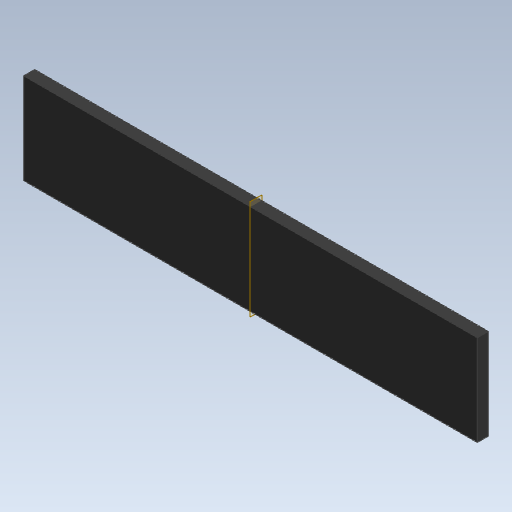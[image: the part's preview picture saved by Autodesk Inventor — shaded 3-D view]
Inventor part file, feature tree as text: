
AUTODESK INVENTOR PART (.ipt)
format: ipt  version: 2020 (Build 240168000, 168)  size: 105,472 bytes
history: native  units: mm
features: other x1, extrude x1
ambient origin geometry x8: Origin, YZ Plane, XZ Plane, XY Plane, X Axis, Y Axis, Z Axis, Center Point
bodies: Body1 (feature_tree)
feature tree (2):
  other  "實體1"
  extrude  "擠出1"  Depth=25.0mm
